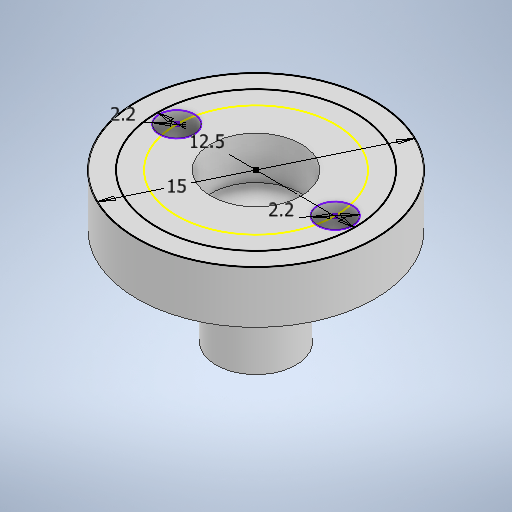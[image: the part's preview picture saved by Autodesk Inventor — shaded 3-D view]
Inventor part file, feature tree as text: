
AUTODESK INVENTOR PART (.ipt)
format: ipt  version: 2025.2 (Build 292293000, 293)  size: 655,360 bytes
history: native  units: in
note: dims shown in document units (in); Inventor stores cm internally (conversion verified against a paired STEP export)
features: extrude x6, sketch x6, fillet x1
ambient origin geometry x8: Origin, YZ Plane, XZ Plane, XY Plane, X Axis, Y Axis, Z Axis, Center Point
bodies: Solid1 (feature_tree)
feature tree (13):
  extrude  "Extrusion1"  Depth=0.1575in TaperAngle=0.0deg
  extrude  "Extrusion2"  Depth=0.0787in TaperAngle=0.0deg
  fillet  "Fillet1"  Radius=0.0787in
  sketch  "Sketch3"  dims[d7=0.5906in d8=0.4921in]
  extrude  "Extrusion3"  Depth=0.4921in
  extrude  "Extrusion4"  Depth=0.0866in
  extrude  "Extrusion5"  Depth=0.2126in TaperAngle=0.0deg
  sketch  "Sketch5"  dims[d11=0.1299in d12=0.0in d13=0.2126in d14=0.0in]
  extrude  "Extrusion6"  Depth=0.2244in
  sketch  "Sketch1"  dims[d0=0.1988in d1=0.1575in d2=0.0in]
  sketch  "Sketch2"  dims[d3=0.3937in d4=0.2126in d5=0.0in d6=0.0787in]
  sketch  "Sketch4"  dims[d9=0.0866in d10=0.0866in]
  sketch  "Sketch6"  dims[d15=0.1299in d16=0.0in d17=0.2244in d18=0.1063in d19=0.0in]
